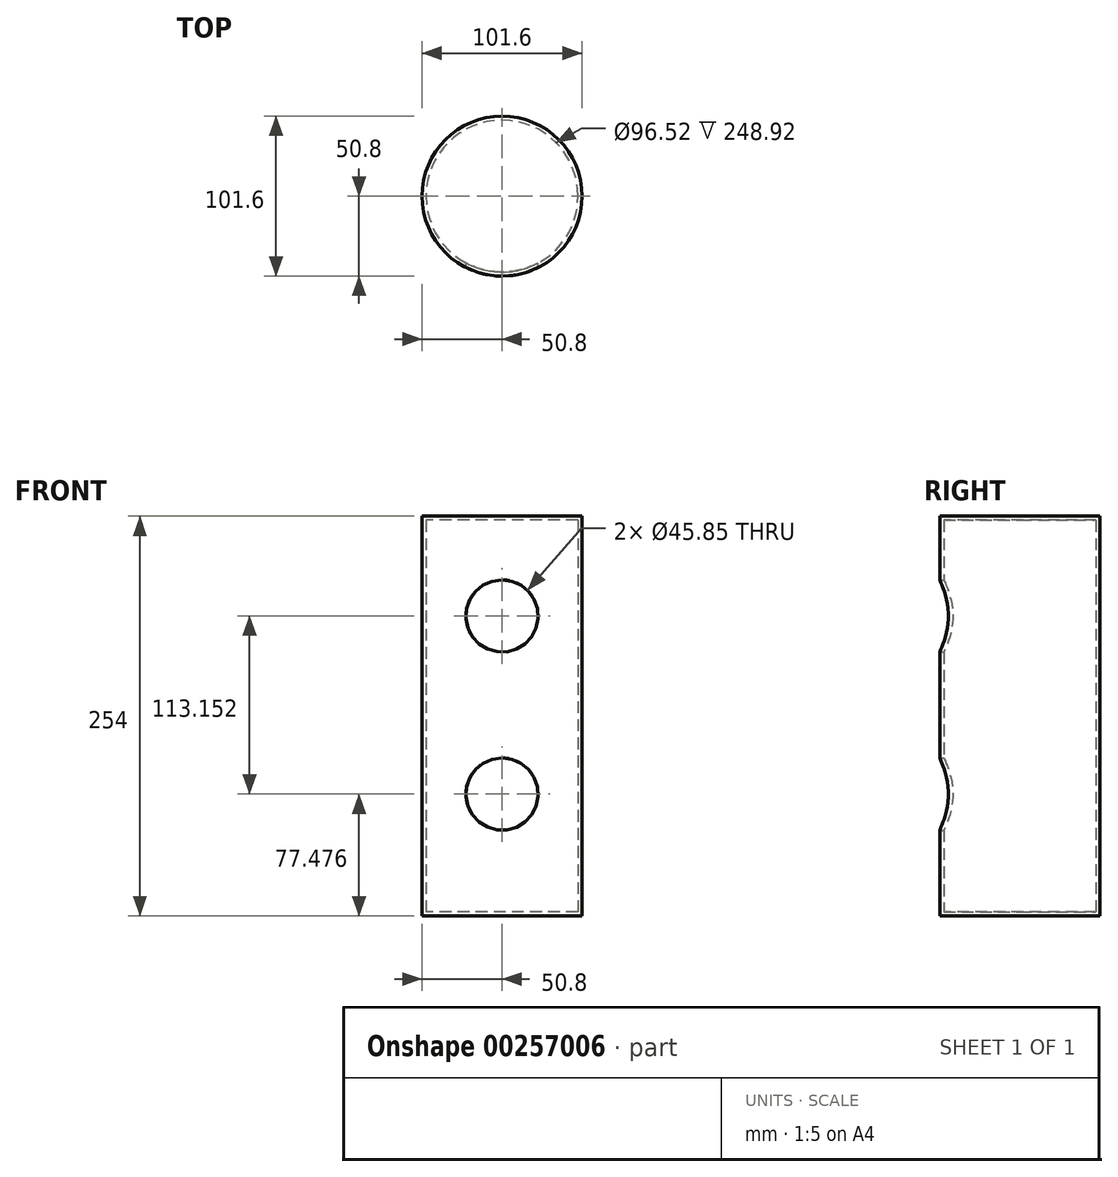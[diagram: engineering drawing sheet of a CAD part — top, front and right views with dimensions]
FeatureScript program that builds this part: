
annotation { "Feature Type Name" : "Feature", "Feature Type Description" : "" }
export const myFeature = defineFeature(function(context is Context, id is Id, definition is map)
    precondition{}
    {
        {
            var Q0;
            Q0=qCreatedBy(makeId("Top.planeOp"),FACE);
            var sketch = newSketch(context, id + "F0", { "sketchPlane" : qUnion([Q0])});
            skCircle(sketch, "E0", {"center": v(0, 0) * mm, "radius": 50.8 * mm});
            skSolve(sketch);
        }
        {
            var Q0;
            Q0 = qSketchRegion(id + "F0", true);
            extrude(context, id + "F1", {"entities" : qUnion([Q0]), "depth" : 254 * mm});
        }
        {
            var Q0;
            Q0=makeQuery(id+"F1.opExtrude","SWEPT_FACE",FACE,{"disambiguationData":[OSD([sQuery(id+"F0.wireOp",EDGE,"E0")])]});
            var Q1;
            Q1=makeQuery(id+"F1.opExtrude","SWEPT_BODY",BODY,{"disambiguationData":[OSD([sQuery(id+"F0.wireOp",EDGE,"E0")])]});
            shell(context, id + "F2", {"isHollow" : true, "entities" : qUnion([Q0]), "parts" : qUnion([Q1]), "thickness" : 2.54 * mm});
        }
        {
            var Q0;
            Q0=qCreatedBy(makeId("Front.planeOp"),FACE);
            var sketch = newSketch(context, id + "F3", { "sketchPlane" : qUnion([Q0])});
            skCircle(sketch, "E1", {"center": v(0, 190.63) * mm, "radius": 22.93 * mm});
            skSolve(sketch);
        }
        {
            var Q0;
            Q0 = qSketchRegion(id + "F3", true);
            extrude(context, id + "F4", {"entities" : qUnion([Q0]), "operationType" : NewBodyOperationType.REMOVE, "depth" : 152.9 * mm});
        }
        {
            var Q0;
            Q0=qCreatedBy(makeId("Front.planeOp"),FACE);
            var sketch = newSketch(context, id + "F5", { "sketchPlane" : qUnion([Q0])});
            skCircle(sketch, "E2", {"center": v(0, 77.48) * mm, "radius": 22.92 * mm});
            skSolve(sketch);
        }
        {
            var Q0;
            Q0 = qSketchRegion(id + "F5", true);
            extrude(context, id + "F6", {"entities" : qUnion([Q0]), "operationType" : NewBodyOperationType.REMOVE, "depth" : 92.2 * mm});
        }
    });
